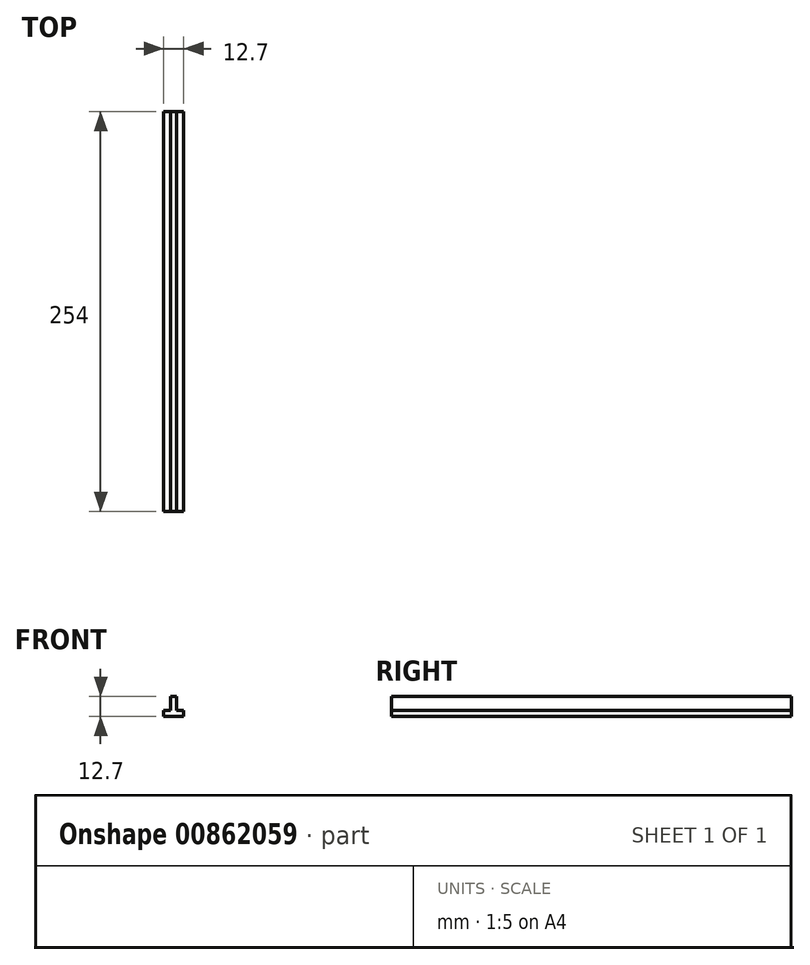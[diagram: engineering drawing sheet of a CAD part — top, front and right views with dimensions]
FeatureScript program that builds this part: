
annotation { "Feature Type Name" : "Feature", "Feature Type Description" : "" }
export const myFeature = defineFeature(function(context is Context, id is Id, definition is map)
    precondition{}
    {
        {
            var Q0;
            Q0=qCreatedBy(makeId("Front.planeOp"),FACE);
            var sketch = newSketch(context, id + "F0", { "sketchPlane" : qUnion([Q0])});
            skLineSegment(sketch, "E0", {"start": v(4.27, 5.33) * mm, "end": v(8.08, 5.33) * mm});
            skLineSegment(sketch, "E1", {"start": v(8.08, 5.33) * mm, "end": v(8.08, -3.56) * mm});
            skLineSegment(sketch, "E2", {"start": v(8.08, -3.56) * mm, "end": v(12.53, -3.56) * mm});
            skLineSegment(sketch, "E3", {"start": v(12.53, -3.56) * mm, "end": v(12.53, -7.37) * mm});
            skLineSegment(sketch, "E4", {"start": v(12.53, -7.37) * mm, "end": v(-0.17, -7.37) * mm});
            skLineSegment(sketch, "E5", {"start": v(-0.17, -7.37) * mm, "end": v(-0.17, -3.56) * mm});
            skLineSegment(sketch, "E6", {"start": v(-0.17, -3.56) * mm, "end": v(4.27, -3.56) * mm});
            skLineSegment(sketch, "E7", {"start": v(4.27, -3.56) * mm, "end": v(4.27, 5.33) * mm});
            skSolve(sketch);
        }
        {
            var Q0;
            Q0=makeQuery(id+"F0.imprint","IMPRINT",FACE,{"disambiguationData":[TD([[makeQuery(id+"F0.imprint","IMPRINT",EDGE,{"derivedFrom":sQuery(id+"F0.wireOp",EDGE,"E0")}),-1.0]])]});
            extrude(context, id + "F1", {"entities" : qUnion([Q0]), "depth" : 254 * mm, "offsetDistance" : 25.4 * mm});
        }
    });
